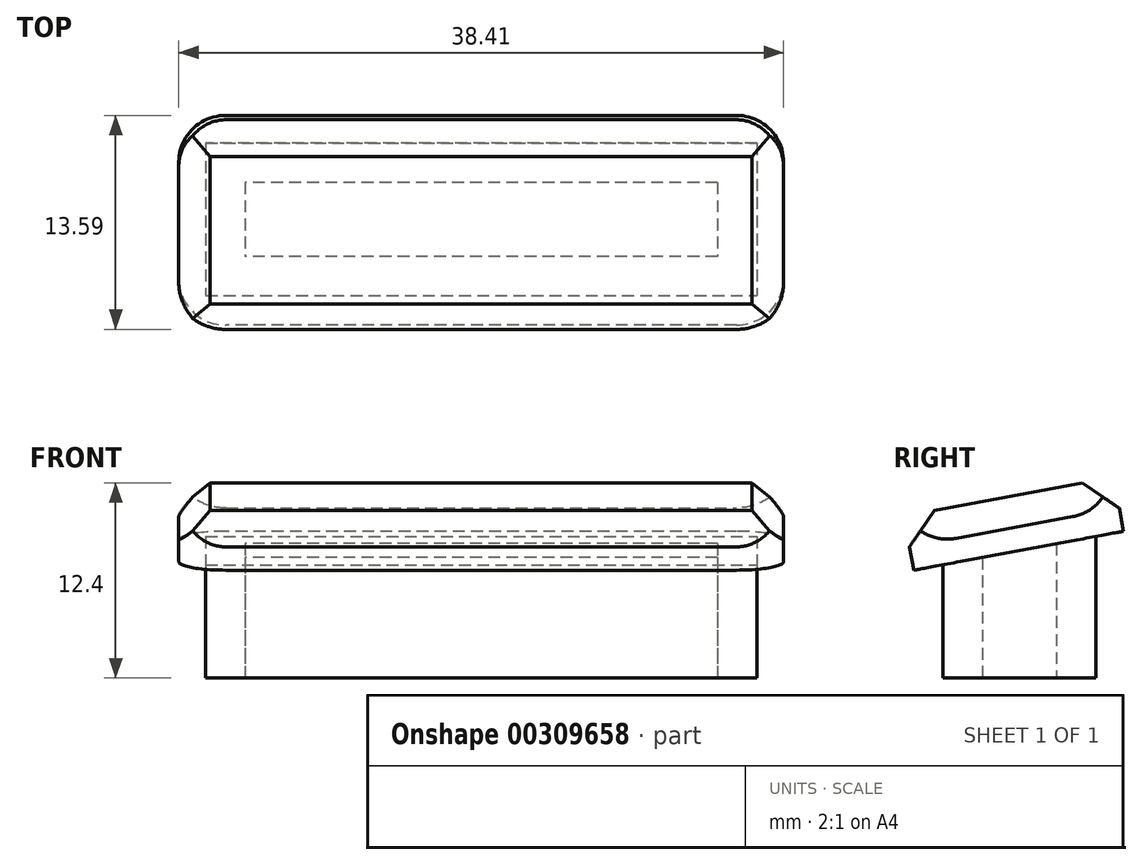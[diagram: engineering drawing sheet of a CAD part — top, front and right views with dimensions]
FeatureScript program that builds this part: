
annotation { "Feature Type Name" : "Feature", "Feature Type Description" : "" }
export const myFeature = defineFeature(function(context is Context, id is Id, definition is map)
    precondition{}
    {
        {
            var Q0;
            Q0=qCreatedBy(makeId("Top.planeOp"),FACE);
            var sketch = newSketch(context, id + "F0", { "sketchPlane" : qUnion([Q0])});
            skLineSegment(sketch, "E0.bottom", {"start": v(19.5, 7) * mm, "end": v(-19.5, 7) * mm});
            skLineSegment(sketch, "E0.top", {"start": v(19.5, -7) * mm, "end": v(-19.5, -7) * mm});
            skLineSegment(sketch, "E0.left", {"start": v(19.5, 7) * mm, "end": v(19.5, -7) * mm});
            skLineSegment(sketch, "E0.right", {"start": v(-19.5, 7) * mm, "end": v(-19.5, -7) * mm});
            skPoint(sketch, "E0.middle", {"position": v(0, 0) * mm});
            skSolve(sketch);
        }
        {
            var Q0;
            Q0 = qSketchRegion(id + "F0", true);
            extrude(context, id + "F1", {"entities" : qUnion([Q0]), "depth" : 3.5 * mm});
        }
        {
            var Q0;
            Q0=makeQuery(id+"F1.opExtrude","CAP_FACE",FACE,{"disambiguationData":[OSD([sQuery(id+"F0.wireOp",EDGE,"E0.bottom"),sQuery(id+"F0.wireOp",EDGE,"E0.top"),sQuery(id+"F0.wireOp",EDGE,"E0.left"),sQuery(id+"F0.wireOp",EDGE,"E0.right")])],"isStart":false});
            var sketch = newSketch(context, id + "F2", { "sketchPlane" : qUnion([Q0])});
            skLineSegment(sketch, "E1.bottom", {"start": v(17.5, 4.85) * mm, "end": v(-17.5, 4.85) * mm});
            skLineSegment(sketch, "E1.top", {"start": v(17.5, -4.85) * mm, "end": v(-17.5, -4.85) * mm});
            skLineSegment(sketch, "E1.left", {"start": v(17.5, 4.85) * mm, "end": v(17.5, -4.85) * mm});
            skLineSegment(sketch, "E1.right", {"start": v(-17.5, 4.85) * mm, "end": v(-17.5, -4.85) * mm});
            skPoint(sketch, "E1.middle", {"position": v(0, 0) * mm});
            skLineSegment(sketch, "E2.bottom", {"start": v(15, 2.35) * mm, "end": v(-15, 2.35) * mm});
            skLineSegment(sketch, "E2.top", {"start": v(15, -2.35) * mm, "end": v(-15, -2.35) * mm});
            skLineSegment(sketch, "E2.left", {"start": v(15, 2.35) * mm, "end": v(15, -2.35) * mm});
            skLineSegment(sketch, "E2.right", {"start": v(-15, 2.35) * mm, "end": v(-15, -2.35) * mm});
            skSolve(sketch);
        }
        {
            var Q0;
            Q0 = qSketchRegion(id + "F2", true);
            extrude(context, id + "F3", {"entities" : qUnion([Q0]), "operationType" : NewBodyOperationType.ADD, "depth" : 9 * mm});
        }
        {
            var Q0;
            Q0=qCreatedBy(makeId("Right.planeOp"),FACE);
            var sketch = newSketch(context, id + "F4", { "sketchPlane" : qUnion([Q0])});
            skLineSegment(sketch, "E3", {"start": v(4.85, 12.5) * mm, "end": v(-4.85, 10.7) * mm});
            skLineSegment(sketch, "E4", {"start": v(-4.85, 10.7) * mm, "end": v(-5.26, 12.88) * mm});
            skLineSegment(sketch, "E5", {"start": v(-5.26, 12.88) * mm, "end": v(4.85, 12.5) * mm});
            skSolve(sketch);
        }
        {
            var Q0;
            Q0 = qSketchRegion(id + "F4", true);
            extrude(context, id + "F5", {"entities" : qUnion([Q0]), "operationType" : NewBodyOperationType.REMOVE, "endBound" : BoundingType.SYMMETRIC, "oppositeDirection" : true, "depth" : 45 * mm});
        }
        {
            var Q0;
            Q0=makeQuery(id+"F5.boolean.opBoolean","COPY",FACE,{"derivedFrom":makeQuery(id+"F5.opExtrude","SWEPT_FACE",FACE,{"disambiguationData":[OSD([sQuery(id+"F4.wireOp",EDGE,"E3")])]})});
            var sketch = newSketch(context, id + "F6", { "sketchPlane" : qUnion([Q0])});
            skLineSegment(sketch, "E6.bottom", {"start": v(19.2, 8.83) * mm, "end": v(-19.2, 8.83) * mm});
            skPoint(sketch, "E6.middle", {"position": v(0, -0.75) * mm});
            skLineSegment(sketch, "E7.bottom", {"start": v(19.2, -4.72) * mm, "end": v(-19.2, -4.72) * mm});
            skLineSegment(sketch, "E7.left", {"start": v(19.2, -4.72) * mm, "end": v(19.2, 8.83) * mm});
            skLineSegment(sketch, "E7.right", {"start": v(-19.2, -4.72) * mm, "end": v(-19.2, 8.83) * mm});
            skSolve(sketch);
        }
        {
            var Q0;
            Q0 = qSketchRegion(id + "F6", true);
            extrude(context, id + "F7", {"entities" : qUnion([Q0]), "operationType" : NewBodyOperationType.ADD, "depth" : 3.5 * mm});
        }
        {
            var Q0;
            Q0=makeQuery(id+"F7.opExtrude","CAP_FACE",FACE,{"disambiguationData":[OSD([sQuery(id+"F6.wireOp",EDGE,"E6.bottom"),sQuery(id+"F6.wireOp",EDGE,"E7.bottom"),sQuery(id+"F6.wireOp",EDGE,"E7.left"),sQuery(id+"F6.wireOp",EDGE,"E7.right")])],"isStart":false});
            chamfer(context, id + "F8", {"entities" : qUnion([Q0]), "width" : 2 * mm, "tangentPropagation" : true});
        }
        {
            var Q0;
            Q0=makeQuery(id+"F7.opExtrude","SWEPT_EDGE",EDGE,{"disambiguationData":[OSD([sQuery(id+"F6.wireOp",EDGE,"E7.bottom"),sQuery(id+"F6.wireOp",EDGE,"E7.left")])]});
            var Q1;
            Q1=makeQuery(id+"F7.opExtrude","SWEPT_EDGE",EDGE,{"disambiguationData":[OSD([sQuery(id+"F6.wireOp",EDGE,"E6.bottom"),sQuery(id+"F6.wireOp",EDGE,"E7.left")])]});
            var Q2;
            Q2=makeQuery(id+"F7.opExtrude","SWEPT_EDGE",EDGE,{"disambiguationData":[OSD([sQuery(id+"F6.wireOp",EDGE,"E6.bottom"),sQuery(id+"F6.wireOp",EDGE,"E7.right")])]});
            var Q3;
            Q3=makeQuery(id+"F7.opExtrude","SWEPT_EDGE",EDGE,{"disambiguationData":[OSD([sQuery(id+"F6.wireOp",EDGE,"E7.bottom"),sQuery(id+"F6.wireOp",EDGE,"E7.right")])]});
            fillet(context, id + "F9", {"entities" : qUnion([Q0, Q1, Q2, Q3]), "radius" : 3 * mm, "tangentPropagation" : true, "allowEdgeOverflow" : false});
        }
        {
            var Q0;
            Q0=makeQuery(id+"F1.opExtrude","SWEPT_FACE",FACE,{"disambiguationData":[OSD([sQuery(id+"F0.wireOp",EDGE,"E0.right")])]});
            extrude(context, id + "F10", {"entities" : qUnion([Q0]), "operationType" : NewBodyOperationType.REMOVE, "endBound" : BoundingType.THROUGH_ALL, "oppositeDirection" : true, "depth" : 25 * mm});
        }
    });
